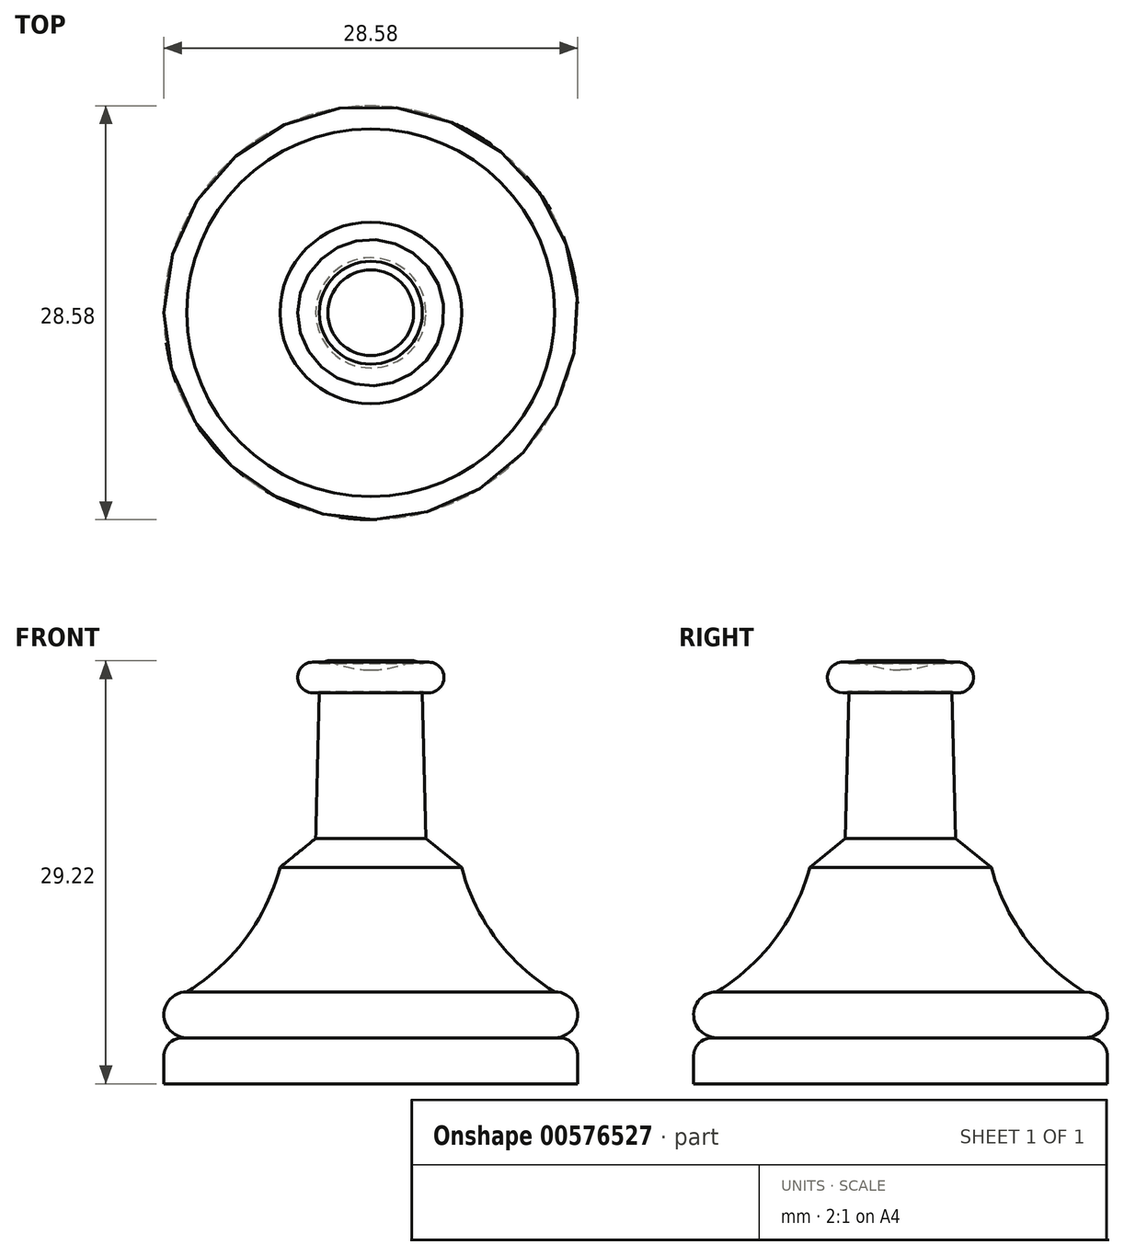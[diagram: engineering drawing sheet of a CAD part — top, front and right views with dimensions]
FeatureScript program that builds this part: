
annotation { "Feature Type Name" : "Feature", "Feature Type Description" : "" }
export const myFeature = defineFeature(function(context is Context, id is Id, definition is map)
    precondition{}
    {
        {
            var Q0;
            Q0=qCreatedBy(makeId("Front.planeOp"),FACE);
            var sketch = newSketch(context, id + "F0", { "sketchPlane" : qUnion([Q0])});
            skLineSegment(sketch, "E0", {"start": v(0, 0) * mm, "end": v(0, 44.45) * mm});
            skLineSegment(sketch, "E1", {"start": v(0, 0) * mm, "end": v(14.29, 0) * mm});
            skLineSegment(sketch, "E2", {"start": v(14.29, 0) * mm, "end": v(14.29, 3.17) * mm});
            skLineSegment(sketch, "E3", {"start": v(14.29, 3.17) * mm, "end": v(12.7, 3.17) * mm});
            skArc(sketch, "E4", {"start": v(12.7, 3.17) * mm, "mid": v(14.29, 4.76) * mm, "end": v(12.7, 6.35) * mm});
            skLineSegment(sketch, "E5", {"start": v(3.8, 16.95) * mm, "end": v(3.55, 27.1) * mm});
            skArc(sketch, "E6", {"start": v(3.55, 27.1) * mm, "mid": v(5.05, 28.07) * mm, "end": v(3.55, 29.03) * mm});
            skLineSegment(sketch, "E7", {"start": v(3.55, 29.03) * mm, "end": v(3.55, 29.03) * mm});
            skPoint(sketch, "E8.startSnap0", {"position": v(5.05, 28.07) * mm});
            skPoint(sketch, "E9.orphan", {"position": v(0, 28.07) * mm});
            skArc(sketch, "E10", {"start": v(0, 28.58) * mm, "mid": v(7.76, 36.51) * mm, "end": v(0, 44.45) * mm});
            skLineSegment(sketch, "E11", {"start": v(3.8, 16.95) * mm, "end": v(6.27, 14.94) * mm});
            skLineSegment(sketch, "E12", {"start": v(3.55, 29.03) * mm, "end": v(2.96, 29.22) * mm});
            skArc(sketch, "E13", {"start": v(6.27, 14.94) * mm, "mid": v(8.65, 10.02) * mm, "end": v(12.7, 6.35) * mm});
            skLineSegment(sketch, "E14", {"start": v(3.8, 16.95) * mm, "end": v(0, 16.85) * mm});
            skLineSegment(sketch, "E15", {"start": v(3.55, 27.1) * mm, "end": v(0, 27.02) * mm});
            skSolve(sketch);
        }
        {
            var Q0;
            {var subQ0=sQuery(id+"F0.wireOp",EDGE,"E10");var subQ1=sQuery(id+"F0.wireOp",EDGE,"E0");var subQ2=makeQuery(id+"F0.imprint","INTERSECT",VERTEX,{"disambiguationData":[OD(0.0)],"derivedFrom":[subQ1,subQ0]});Q0=makeQuery(id+"F0.imprint","IMPRINT",FACE,{"disambiguationData":[TD([[makeQuery(id+"F0.imprint","IMPRINT",EDGE,{"disambiguationData":[TD([[subQ2,1.0]])],"derivedFrom":subQ1}),-1.0]])]});}
            var Q1;
            {var subQ4=sQuery(id+"F0.wireOp",EDGE,"E1");Q1=makeQuery(id+"F0.imprint","IMPRINT",FACE,{"disambiguationData":[TD([[makeQuery(id+"F0.imprint","IMPRINT",EDGE,{"derivedFrom":subQ4}),1.0]])]});}
            var Q2;
            Q2=makeQuery(id+"F0.imprint","IMPRINT",FACE,{"disambiguationData":[TD([[makeQuery(id+"F0.imprint","IMPRINT",EDGE,{"derivedFrom":sQuery(id+"F0.wireOp",EDGE,"E5")}),1.0]])]});
            var Q3;
            Q3=makeQuery(id+"F0.imprint","IMPRINT",FACE,{"disambiguationData":[TD([[makeQuery(id+"F0.imprint","IMPRINT",EDGE,{"derivedFrom":sQuery(id+"F0.wireOp",EDGE,"E6")}),1.0]])]});
            var Q4;
            Q4=sQuery(id+"F0.wireOp",EDGE,"E0");
            revolve(context, id + "F1", {"entities" : qUnion([Q0, Q1, Q2, Q3]), "axis" : qUnion([Q4]), "revolveType" : RevolveType.FULL});
        }
        {
            var Q0;
            Q0=makeQuery(id+"F1.opRevolve","SWEPT_EDGE",EDGE,{"disambiguationData":[OSD([sQuery(id+"F0.wireOp",EDGE,"E2"),sQuery(id+"F0.wireOp",EDGE,"E3")])]});
            fillet(context, id + "F2", {"entities" : qUnion([Q0]), "radius" : 1.27 * mm, "tangentPropagation" : true, "allowEdgeOverflow" : false});
        }
    });
